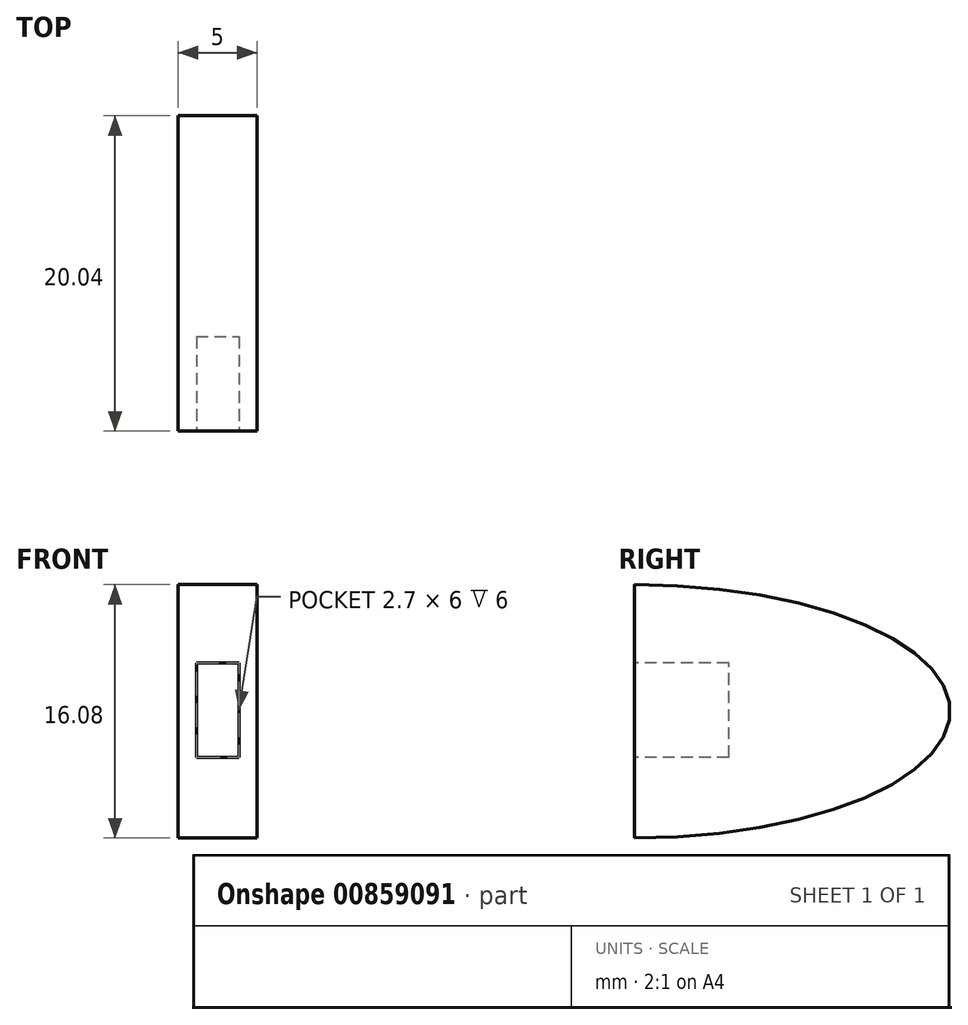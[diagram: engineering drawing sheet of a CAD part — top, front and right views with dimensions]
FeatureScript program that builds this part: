
annotation { "Feature Type Name" : "Feature", "Feature Type Description" : "" }
export const myFeature = defineFeature(function(context is Context, id is Id, definition is map)
    precondition{}
    {
        {
            var Q0;
            Q0=qCreatedBy(makeId("Right.planeOp"),FACE);
            var sketch = newSketch(context, id + "F0", { "sketchPlane" : qUnion([Q0])});
            skEllipticalArc(sketch, "E0", {});
            skLineSegment(sketch, "E1", {"start": v(0, 13.26) * mm, "end": v(0, -2.82) * mm});
            const initialGuessF0  = {"E0": [0, 0.005222120399903239, 1, 0, 0.020039424300193787, 0.008042818647943442, 4.71238898038469, 1.5707963267948966]};
            skSetInitialGuess(sketch, initialGuessF0);
            skSolve(sketch);
        }
        {
            var Q0;
            Q0 = qSketchRegion(id + "F0", true);
            extrude(context, id + "F1", {"entities" : qUnion([Q0]), "endBound" : BoundingType.SYMMETRIC, "depth" : 5 * mm, "offsetDistance" : 25 * mm});
        }
        {
            var Q0;
            Q0=qCreatedBy(makeId("Front.planeOp"),FACE);
            var sketch = newSketch(context, id + "F2", { "sketchPlane" : qUnion([Q0])});
            skLineSegment(sketch, "E2.bottom", {"start": v(-1.35, 2.3) * mm, "end": v(1.35, 2.3) * mm});
            skLineSegment(sketch, "E2.top", {"start": v(-1.35, 8.3) * mm, "end": v(1.35, 8.3) * mm});
            skLineSegment(sketch, "E2.left", {"start": v(-1.35, 2.3) * mm, "end": v(-1.35, 8.3) * mm});
            skLineSegment(sketch, "E2.right", {"start": v(1.35, 2.3) * mm, "end": v(1.35, 8.3) * mm});
            skPoint(sketch, "E2.middle", {"position": v(0, 5.3) * mm});
            skSolve(sketch);
        }
        {
            var Q0;
            Q0 = qSketchRegion(id + "F2", true);
            extrude(context, id + "F3", {"entities" : qUnion([Q0]), "operationType" : NewBodyOperationType.REMOVE, "oppositeDirection" : true, "depth" : 6 * mm, "offsetDistance" : 25 * mm});
        }
    });
